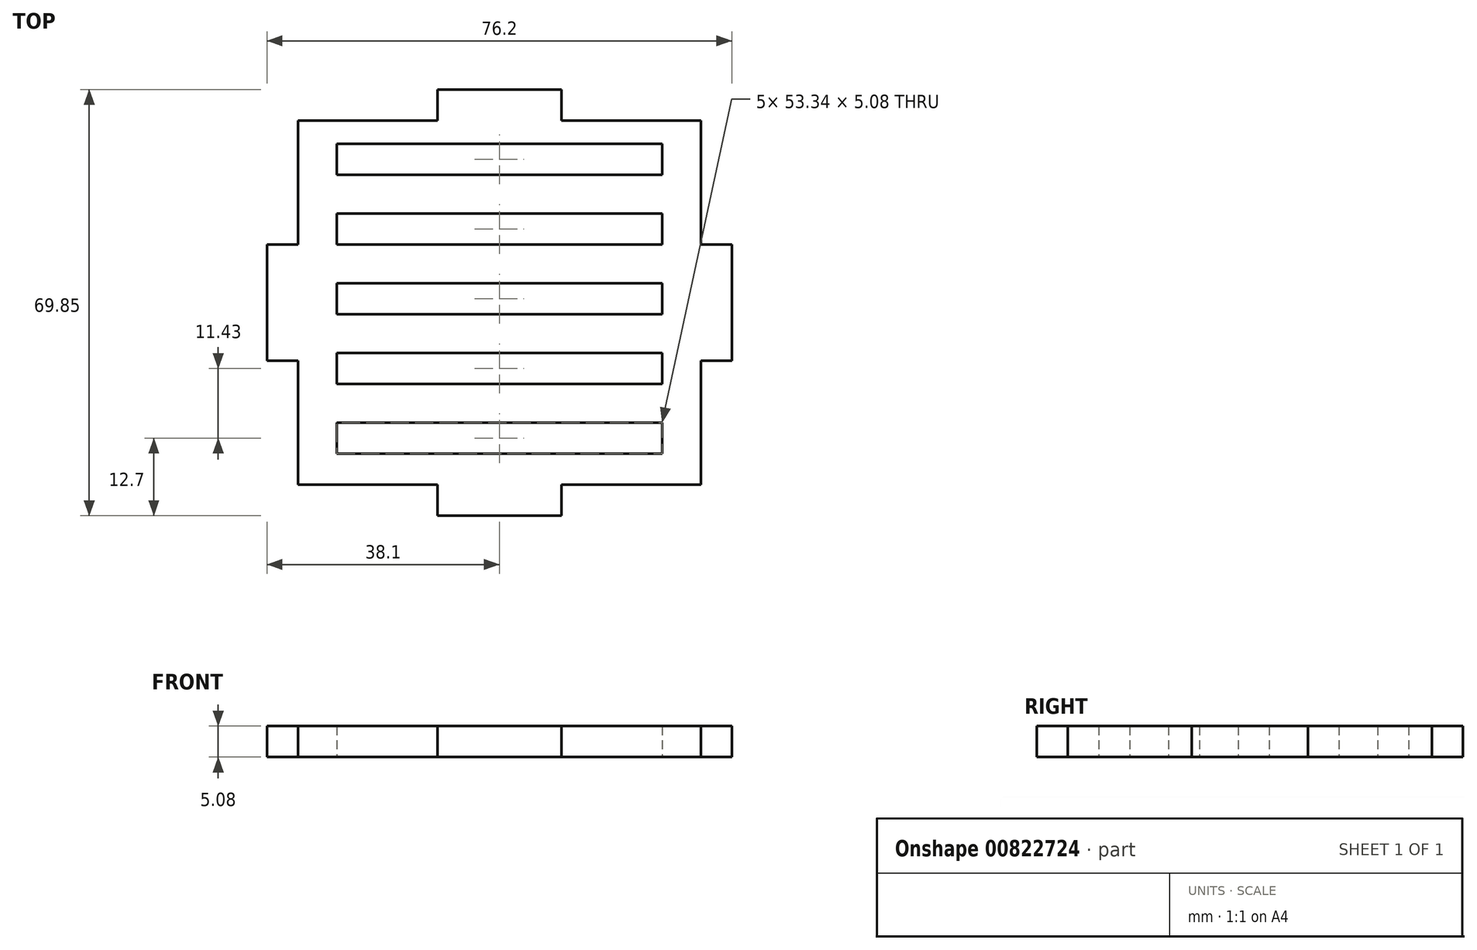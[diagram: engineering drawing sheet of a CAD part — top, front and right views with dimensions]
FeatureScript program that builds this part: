
annotation { "Feature Type Name" : "Feature", "Feature Type Description" : "" }
export const myFeature = defineFeature(function(context is Context, id is Id, definition is map)
    precondition{}
    {
        {
            var Q0;
            Q0=qCreatedBy(makeId("Top.planeOp"),FACE);
            var sketch = newSketch(context, id + "F0", { "sketchPlane" : qUnion([Q0])});
            skLineSegment(sketch, "E0.bottom", {"start": v(27.94, 0) * mm, "end": v(48.26, 0) * mm});
            skLineSegment(sketch, "E0.top", {"start": v(27.94, -69.85) * mm, "end": v(48.26, -69.85) * mm});
            skLineSegment(sketch, "E0.left", {"start": v(0, -25.4) * mm, "end": v(0, -44.45) * mm});
            skLineSegment(sketch, "E1", {"start": v(5.08, -5.08) * mm, "end": v(27.94, -5.08) * mm});
            skLineSegment(sketch, "E2", {"start": v(27.94, -5.08) * mm, "end": v(27.94, 0) * mm});
            skLineSegment(sketch, "E3", {"start": v(48.26, 0) * mm, "end": v(48.26, -5.08) * mm});
            skLineSegment(sketch, "E4", {"start": v(48.26, -5.08) * mm, "end": v(71.12, -5.08) * mm});
            skPoint(sketch, "E5.orphan", {"position": v(0, 0) * mm});
            skPoint(sketch, "E6.orphan", {"position": v(76.2, 0) * mm});
            skLineSegment(sketch, "E7", {"start": v(5.08, -5.08) * mm, "end": v(5.08, -25.4) * mm});
            skLineSegment(sketch, "E8", {"start": v(5.08, -25.4) * mm, "end": v(0, -25.4) * mm});
            skLineSegment(sketch, "E9", {"start": v(0, -44.45) * mm, "end": v(5.08, -44.45) * mm});
            skLineSegment(sketch, "E10", {"start": v(5.08, -44.45) * mm, "end": v(5.08, -64.77) * mm});
            skLineSegment(sketch, "E11", {"start": v(5.08, -64.77) * mm, "end": v(27.94, -64.77) * mm});
            skLineSegment(sketch, "E12", {"start": v(27.94, -64.77) * mm, "end": v(27.94, -69.85) * mm});
            skPoint(sketch, "E13.orphan", {"position": v(0, -69.85) * mm});
            skLineSegment(sketch, "E14", {"start": v(38.1, 0) * mm, "end": v(38.1, -3.81) * mm, "construction": true});
            skLineSegment(sketch, "E15.MirrorCS", {"start": v(71.12, -5.08) * mm, "end": v(71.12, -25.4) * mm});
            skLineSegment(sketch, "E16.MirrorCS", {"start": v(71.12, -25.4) * mm, "end": v(76.2, -25.4) * mm});
            skLineSegment(sketch, "E17.MirrorCS", {"start": v(76.2, -25.4) * mm, "end": v(76.2, -44.45) * mm});
            skLineSegment(sketch, "E18.MirrorCS", {"start": v(76.2, -44.45) * mm, "end": v(71.12, -44.45) * mm});
            skLineSegment(sketch, "E19.MirrorCS", {"start": v(71.12, -44.45) * mm, "end": v(71.12, -64.77) * mm});
            skLineSegment(sketch, "E20.MirrorCS", {"start": v(71.12, -64.77) * mm, "end": v(48.26, -64.77) * mm});
            skLineSegment(sketch, "E21", {"start": v(48.26, -64.77) * mm, "end": v(48.26, -69.85) * mm});
            skLineSegment(sketch, "E22.bottom", {"start": v(11.43, -8.9) * mm, "end": v(64.77, -8.9) * mm});
            skLineSegment(sketch, "E22.top", {"start": v(11.43, -13.97) * mm, "end": v(64.77, -13.97) * mm});
            skLineSegment(sketch, "E22.left", {"start": v(11.43, -8.9) * mm, "end": v(11.43, -13.97) * mm});
            skLineSegment(sketch, "E22.right", {"start": v(64.77, -8.9) * mm, "end": v(64.77, -13.97) * mm});
            skLineSegment(sketch, "E23.bottom", {"start": v(11.43, -20.32) * mm, "end": v(64.77, -20.32) * mm});
            skLineSegment(sketch, "E23.top", {"start": v(11.43, -25.4) * mm, "end": v(64.77, -25.4) * mm});
            skLineSegment(sketch, "E23.left", {"start": v(11.43, -20.32) * mm, "end": v(11.43, -25.4) * mm});
            skLineSegment(sketch, "E23.right", {"start": v(64.77, -20.32) * mm, "end": v(64.77, -25.4) * mm});
            skLineSegment(sketch, "E24.bottom", {"start": v(11.43, -31.75) * mm, "end": v(64.77, -31.75) * mm});
            skLineSegment(sketch, "E24.top", {"start": v(11.43, -36.83) * mm, "end": v(64.77, -36.83) * mm});
            skLineSegment(sketch, "E24.left", {"start": v(11.43, -31.75) * mm, "end": v(11.43, -36.83) * mm});
            skLineSegment(sketch, "E24.right", {"start": v(64.77, -31.75) * mm, "end": v(64.77, -36.83) * mm});
            skLineSegment(sketch, "E25.bottom", {"start": v(11.43, -43.18) * mm, "end": v(64.77, -43.18) * mm});
            skLineSegment(sketch, "E25.top", {"start": v(11.43, -48.26) * mm, "end": v(64.77, -48.26) * mm});
            skLineSegment(sketch, "E25.left", {"start": v(11.43, -43.18) * mm, "end": v(11.43, -48.26) * mm});
            skLineSegment(sketch, "E25.right", {"start": v(64.77, -43.18) * mm, "end": v(64.77, -48.26) * mm});
            skLineSegment(sketch, "E26.bottom", {"start": v(11.43, -54.61) * mm, "end": v(64.77, -54.61) * mm});
            skLineSegment(sketch, "E26.top", {"start": v(11.43, -59.7) * mm, "end": v(64.77, -59.7) * mm});
            skLineSegment(sketch, "E26.left", {"start": v(11.43, -54.61) * mm, "end": v(11.43, -59.7) * mm});
            skLineSegment(sketch, "E26.right", {"start": v(64.77, -54.61) * mm, "end": v(64.77, -59.7) * mm});
            skLineSegment(sketch, "E27", {"start": v(11.43, -5.08) * mm, "end": v(11.43, -8.9) * mm, "construction": true});
            skLineSegment(sketch, "E28", {"start": v(11.43, -13.97) * mm, "end": v(11.43, -20.32) * mm, "construction": true});
            skLineSegment(sketch, "E29", {"start": v(11.43, -25.4) * mm, "end": v(11.43, -31.75) * mm, "construction": true});
            skLineSegment(sketch, "E30", {"start": v(11.43, -36.83) * mm, "end": v(11.43, -43.18) * mm, "construction": true});
            skLineSegment(sketch, "E31", {"start": v(11.43, -48.26) * mm, "end": v(11.43, -54.61) * mm, "construction": true});
            skSolve(sketch);
        }
        {
            var Q0;
            Q0=makeQuery(id+"F0.imprint","IMPRINT",FACE,{"disambiguationData":[TD([[makeQuery(id+"F0.imprint","IMPRINT",EDGE,{"derivedFrom":sQuery(id+"F0.wireOp",EDGE,"E0.top")}),1.0]])]});
            extrude(context, id + "F1", {"entities" : qUnion([Q0]), "depth" : 5.08 * mm, "offsetDistance" : 25.4 * mm});
        }
    });
